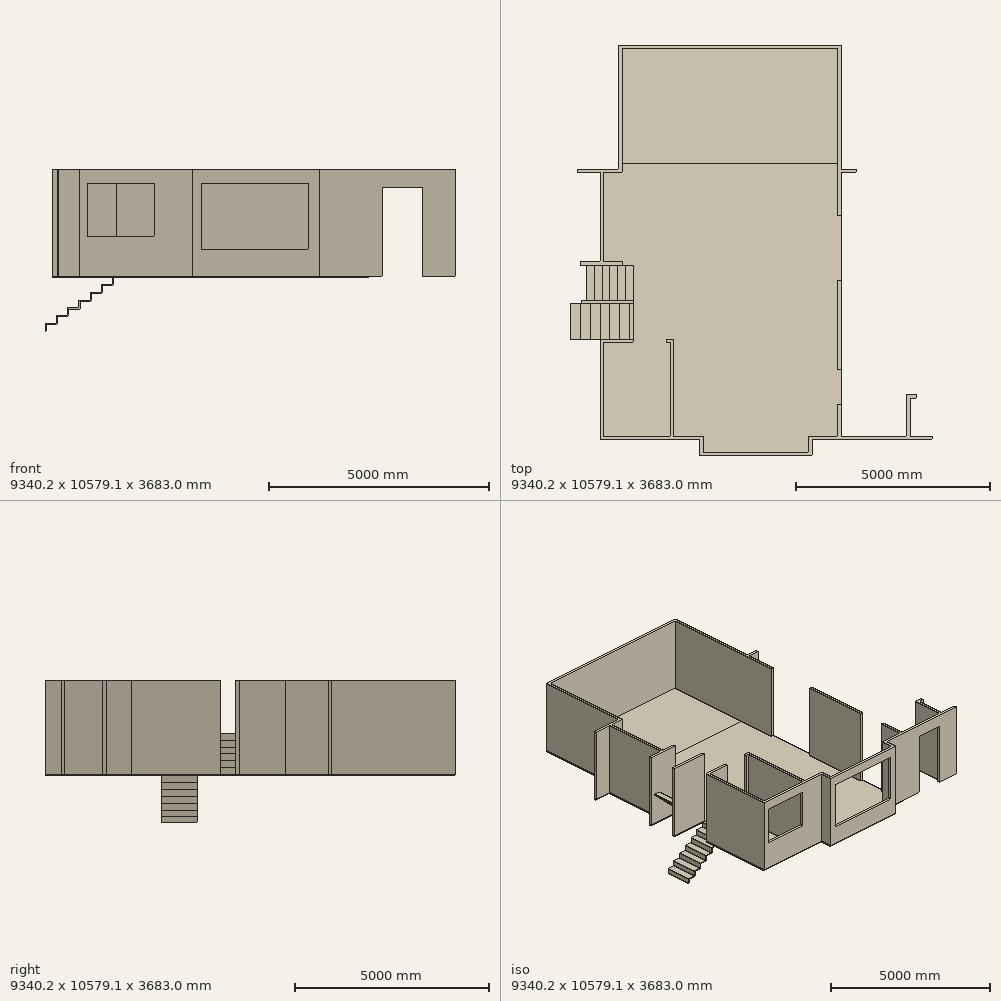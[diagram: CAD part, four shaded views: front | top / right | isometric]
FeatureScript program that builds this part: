
annotation { "Feature Type Name" : "Feature", "Feature Type Description" : "" }
export const myFeature = defineFeature(function(context is Context, id is Id, definition is map)
    precondition{}
    {
        {
            var Q0;
            Q0=qCreatedBy(makeId("Top.planeOp"),FACE);
            var sketch = newSketch(context, id + "F0", { "sketchPlane" : qUnion([Q0])});
            skLineSegment(sketch, "E0", {"start": v(0, 0) * mm, "end": v(0, 2590.8) * mm});
            skLineSegment(sketch, "E1", {"start": v(0, 2590.8) * mm, "end": v(850.9, 2590.8) * mm});
            skLineSegment(sketch, "E2", {"start": v(850.9, 2590.8) * mm, "end": v(850.9, 2501.9) * mm});
            skLineSegment(sketch, "E3", {"start": v(850.9, 2501.9) * mm, "end": v(88.9, 2501.9) * mm});
            skLineSegment(sketch, "E4", {"start": v(88.9, 2501.9) * mm, "end": v(88.9, 88.9) * mm});
            skLineSegment(sketch, "E5", {"start": v(88.9, 88.9) * mm, "end": v(184.15, 88.9) * mm});
            skLineSegment(sketch, "E6", {"start": v(184.15, 88.9) * mm, "end": v(184.15, 0) * mm});
            skLineSegment(sketch, "E7", {"start": v(184.15, 0) * mm, "end": v(0, 0) * mm});
            skLineSegment(sketch, "E8", {"start": v(1708.15, 0) * mm, "end": v(1708.15, 88.9) * mm});
            skLineSegment(sketch, "E9", {"start": v(1708.15, 88.9) * mm, "end": v(1803.4, 88.9) * mm});
            skLineSegment(sketch, "E10", {"start": v(1803.4, 88.9) * mm, "end": v(1803.4, 2501.9) * mm});
            skLineSegment(sketch, "E11", {"start": v(1803.4, 2501.9) * mm, "end": v(1714.5, 2501.9) * mm});
            skLineSegment(sketch, "E12", {"start": v(1714.5, 2501.9) * mm, "end": v(1714.5, 2590.8) * mm});
            skLineSegment(sketch, "E13", {"start": v(1714.5, 2590.8) * mm, "end": v(1892.3, 2590.8) * mm});
            skLineSegment(sketch, "E14", {"start": v(1892.3, 2590.8) * mm, "end": v(1892.3, 88.9) * mm});
            skLineSegment(sketch, "E15", {"start": v(2654.3, -317.5) * mm, "end": v(2654.3, 88.9) * mm});
            skLineSegment(sketch, "E16", {"start": v(2654.3, 88.9) * mm, "end": v(1892.3, 88.9) * mm});
            skLineSegment(sketch, "E17", {"start": v(2654.3, -317.5) * mm, "end": v(2705.1, -317.5) * mm});
            skLineSegment(sketch, "E18", {"start": v(2705.1, -317.5) * mm, "end": v(2705.1, -406.4) * mm});
            skLineSegment(sketch, "E19", {"start": v(2705.1, -406.4) * mm, "end": v(2565.4, -406.4) * mm});
            skLineSegment(sketch, "E20", {"start": v(2565.4, -406.4) * mm, "end": v(2565.4, 0) * mm});
            skLineSegment(sketch, "E21", {"start": v(2565.4, 0) * mm, "end": v(1708.15, 0) * mm});
            skLineSegment(sketch, "E22", {"start": v(184.15, 44.45) * mm, "end": v(1708.15, 44.45) * mm, "construction": true});
            skLineSegment(sketch, "E23", {"start": v(2705.1, -361.95) * mm, "end": v(3924.3, -361.95) * mm, "construction": true});
            skLineSegment(sketch, "E24", {"start": v(4083.05, -361.95) * mm, "end": v(5302.25, -361.95) * mm, "construction": true});
            skLineSegment(sketch, "E25", {"start": v(3924.3, -317.5) * mm, "end": v(4083.05, -317.5) * mm});
            skLineSegment(sketch, "E26", {"start": v(4083.05, -317.5) * mm, "end": v(4083.05, -406.4) * mm});
            skLineSegment(sketch, "E27", {"start": v(4083.05, -406.4) * mm, "end": v(3924.3, -406.4) * mm});
            skLineSegment(sketch, "E28", {"start": v(3924.3, -406.4) * mm, "end": v(3924.3, -317.5) * mm});
            skLineSegment(sketch, "E29", {"start": v(5302.25, -361.95) * mm, "end": v(5302.25, -317.5) * mm});
            skLineSegment(sketch, "E30", {"start": v(5302.25, -317.5) * mm, "end": v(5359.4, -317.5) * mm});
            skLineSegment(sketch, "E31", {"start": v(5359.4, -317.5) * mm, "end": v(5359.4, 88.9) * mm});
            skLineSegment(sketch, "E32", {"start": v(5359.4, 88.9) * mm, "end": v(6121.4, 88.9) * mm});
            skLineSegment(sketch, "E33", {"start": v(6121.4, 88.9) * mm, "end": v(6121.4, 901.7) * mm});
            skLineSegment(sketch, "E34", {"start": v(6121.4, 901.7) * mm, "end": v(6210.3, 901.7) * mm});
            skLineSegment(sketch, "E35", {"start": v(6210.3, 901.7) * mm, "end": v(6210.3, 88.9) * mm});
            skLineSegment(sketch, "E36", {"start": v(6210.3, 88.9) * mm, "end": v(6680.2, 88.9) * mm});
            skLineSegment(sketch, "E37", {"start": v(6680.2, 88.9) * mm, "end": v(6680.2, 0) * mm});
            skLineSegment(sketch, "E38", {"start": v(6680.2, 0) * mm, "end": v(5461, 0) * mm});
            skLineSegment(sketch, "E39", {"start": v(5302.25, -361.95) * mm, "end": v(5302.25, -406.4) * mm});
            skLineSegment(sketch, "E40", {"start": v(5302.25, -406.4) * mm, "end": v(5461, -406.4) * mm});
            skLineSegment(sketch, "E41", {"start": v(5461, -406.4) * mm, "end": v(5461, 0) * mm});
            skLineSegment(sketch, "E42", {"start": v(6680.2, 44.45) * mm, "end": v(7594.6, 44.45) * mm, "construction": true});
            skLineSegment(sketch, "E43", {"start": v(7594.6, 44.45) * mm, "end": v(7594.6, 88.9) * mm});
            skLineSegment(sketch, "E44", {"start": v(7594.6, 88.9) * mm, "end": v(7899.4, 88.9) * mm});
            skLineSegment(sketch, "E45", {"start": v(7899.4, 88.9) * mm, "end": v(7899.4, 1155.7) * mm});
            skLineSegment(sketch, "E46", {"start": v(7899.4, 1155.7) * mm, "end": v(8140.7, 1155.7) * mm});
            skLineSegment(sketch, "E47", {"start": v(8140.7, 1155.7) * mm, "end": v(8140.7, 1066.8) * mm});
            skLineSegment(sketch, "E48", {"start": v(8140.7, 1066.8) * mm, "end": v(7988.3, 1066.8) * mm});
            skLineSegment(sketch, "E49", {"start": v(7988.3, 1066.8) * mm, "end": v(7988.3, 88.9) * mm});
            skLineSegment(sketch, "E50", {"start": v(7988.3, 88.9) * mm, "end": v(8565.55, 88.9) * mm});
            skLineSegment(sketch, "E51", {"start": v(8565.55, 88.9) * mm, "end": v(8565.55, 0) * mm});
            skLineSegment(sketch, "E52", {"start": v(8565.55, 0) * mm, "end": v(7594.6, 0) * mm});
            skLineSegment(sketch, "E53", {"start": v(7594.6, 0) * mm, "end": v(7594.6, 44.45) * mm});
            skLineSegment(sketch, "E54", {"start": v(6165.85, 901.7) * mm, "end": v(6165.85, 1816.1) * mm, "construction": true});
            skLineSegment(sketch, "E55", {"start": v(6165.85, 1816.1) * mm, "end": v(6121.4, 1816.1) * mm});
            skLineSegment(sketch, "E56", {"start": v(6121.4, 1816.1) * mm, "end": v(6121.4, 4102.1) * mm});
            skLineSegment(sketch, "E57", {"start": v(6121.4, 4102.1) * mm, "end": v(6210.3, 4102.1) * mm});
            skLineSegment(sketch, "E58", {"start": v(6210.3, 4102.1) * mm, "end": v(6210.3, 1816.1) * mm});
            skLineSegment(sketch, "E59", {"start": v(6210.3, 1816.1) * mm, "end": v(6165.85, 1816.1) * mm});
            skLineSegment(sketch, "E60", {"start": v(6165.85, 4102.1) * mm, "end": v(6165.85, 5778.5) * mm, "construction": true});
            skLineSegment(sketch, "E61", {"start": v(6165.85, 5778.5) * mm, "end": v(6121.4, 5778.5) * mm});
            skLineSegment(sketch, "E62", {"start": v(6121.4, 5778.5) * mm, "end": v(6121.4, 7200.9) * mm});
            skLineSegment(sketch, "E63", {"start": v(6121.4, 7200.9) * mm, "end": v(6210.3, 7200.9) * mm});
            skLineSegment(sketch, "E64", {"start": v(6210.3, 7200.9) * mm, "end": v(6210.3, 6972.3) * mm});
            skLineSegment(sketch, "E65", {"start": v(6210.3, 6972.3) * mm, "end": v(6608.2, 6972.3) * mm});
            skLineSegment(sketch, "E66", {"start": v(6608.2, 6972.3) * mm, "end": v(6608.2, 6883.4) * mm});
            skLineSegment(sketch, "E67", {"start": v(6608.2, 6883.4) * mm, "end": v(6210.3, 6883.4) * mm});
            skLineSegment(sketch, "E68", {"start": v(6210.3, 6883.4) * mm, "end": v(6210.3, 5778.5) * mm});
            skLineSegment(sketch, "E69", {"start": v(6210.3, 5778.5) * mm, "end": v(6165.85, 5778.5) * mm});
            skLineSegment(sketch, "E70", {"start": v(850.9, 2590.8) * mm, "end": v(850.9, 3505.2) * mm, "construction": true});
            skLineSegment(sketch, "E71", {"start": v(850.9, 3594.1) * mm, "end": v(-482.96, 3594.1) * mm});
            skLineSegment(sketch, "E72", {"start": v(-482.96, 3594.1) * mm, "end": v(-482.96, 3505.2) * mm});
            skLineSegment(sketch, "E73", {"start": v(-482.96, 3505.2) * mm, "end": v(850.9, 3505.2) * mm});
            skLineSegment(sketch, "E74", {"start": v(850.9, 3594.1) * mm, "end": v(850.9, 3505.2) * mm});
            skLineSegment(sketch, "E75", {"start": v(558.8, 3594.1) * mm, "end": v(558.8, 4508.5) * mm, "construction": true});
            skLineSegment(sketch, "E76", {"start": v(558.8, 4508.5) * mm, "end": v(-509.89, 4508.5) * mm});
            skLineSegment(sketch, "E77", {"start": v(-509.89, 4508.5) * mm, "end": v(-509.89, 4597.4) * mm});
            skLineSegment(sketch, "E78", {"start": v(-509.89, 4597.4) * mm, "end": v(0, 4597.4) * mm});
            skLineSegment(sketch, "E79", {"start": v(558.8, 4597.4) * mm, "end": v(558.8, 4508.5) * mm});
            skLineSegment(sketch, "E80", {"start": v(88.9, 4597.4) * mm, "end": v(88.9, 6883.4) * mm});
            skLineSegment(sketch, "E81", {"start": v(88.9, 6883.4) * mm, "end": v(558.8, 6883.4) * mm});
            skLineSegment(sketch, "E82", {"start": v(558.8, 6883.4) * mm, "end": v(558.8, 7200.9) * mm});
            skLineSegment(sketch, "E83", {"start": v(558.8, 7200.9) * mm, "end": v(469.9, 7200.9) * mm});
            skLineSegment(sketch, "E84", {"start": v(469.9, 7200.9) * mm, "end": v(469.9, 6972.3) * mm});
            skLineSegment(sketch, "E85", {"start": v(469.9, 6972.3) * mm, "end": v(-604.12, 6972.3) * mm});
            skLineSegment(sketch, "E86", {"start": v(-604.12, 6972.3) * mm, "end": v(-604.12, 6883.4) * mm});
            skLineSegment(sketch, "E87", {"start": v(-604.12, 6883.4) * mm, "end": v(0, 6883.4) * mm});
            skLineSegment(sketch, "E88", {"start": v(0, 6883.4) * mm, "end": v(0, 4597.4) * mm});
            skLineSegment(sketch, "E89.trimOffspring", {"start": v(88.9, 4597.4) * mm, "end": v(558.8, 4597.4) * mm});
            skLineSegment(sketch, "E90", {"start": v(558.8, 7124.7) * mm, "end": v(6121.4, 7124.7) * mm, "construction": true});
            skLineSegment(sketch, "E91", {"start": v(469.9, 7200.9) * mm, "end": v(469.9, 9029.7) * mm, "construction": true});
            skLineSegment(sketch, "E92", {"start": v(469.9, 9029.7) * mm, "end": v(469.9, 10172.7) * mm});
            skLineSegment(sketch, "E93", {"start": v(558.8, 10083.8) * mm, "end": v(558.8, 9029.7) * mm});
            skLineSegment(sketch, "E94", {"start": v(558.8, 9029.7) * mm, "end": v(469.9, 9029.7) * mm});
            skLineSegment(sketch, "E95", {"start": v(6210.3, 7200.9) * mm, "end": v(6210.3, 9029.7) * mm, "construction": true});
            skLineSegment(sketch, "E96", {"start": v(6210.3, 9029.7) * mm, "end": v(6121.4, 9029.7) * mm});
            skLineSegment(sketch, "E97", {"start": v(6121.4, 9029.7) * mm, "end": v(6121.4, 10083.8) * mm});
            skLineSegment(sketch, "E98", {"start": v(6210.3, 10172.7) * mm, "end": v(6210.3, 9029.7) * mm});
            skLineSegment(sketch, "E99", {"start": v(469.9, 10172.7) * mm, "end": v(6210.3, 10172.7) * mm});
            skLineSegment(sketch, "E100", {"start": v(558.8, 10083.8) * mm, "end": v(6121.4, 10083.8) * mm});
            skLineSegment(sketch, "E101", {"start": v(2705.1, -406.4) * mm, "end": v(5302.25, -406.4) * mm});
            skLineSegment(sketch, "E102", {"start": v(5302.25, -317.5) * mm, "end": v(2705.1, -317.5) * mm});
            skLineSegment(sketch, "E103", {"start": v(1708.15, 0) * mm, "end": v(184.15, 0) * mm});
            skLineSegment(sketch, "E104", {"start": v(1708.15, 88.9) * mm, "end": v(184.15, 88.9) * mm});
            skLineSegment(sketch, "E105", {"start": v(469.9, 7200.9) * mm, "end": v(469.9, 9029.7) * mm});
            skLineSegment(sketch, "E106", {"start": v(558.8, 9029.7) * mm, "end": v(558.8, 7200.9) * mm});
            skLineSegment(sketch, "E107", {"start": v(6121.4, 9029.7) * mm, "end": v(6121.4, 7200.9) * mm});
            skLineSegment(sketch, "E108", {"start": v(6210.3, 7200.9) * mm, "end": v(6210.3, 9029.7) * mm});
            skLineSegment(sketch, "E109", {"start": v(6680.2, 0) * mm, "end": v(7594.6, 0) * mm});
            skLineSegment(sketch, "E110", {"start": v(7594.6, 88.9) * mm, "end": v(6680.2, 88.9) * mm});
            skSolve(sketch);
        }
        {
            var Q0;
            Q0 = qSketchRegion(id + "F0", true);
            extrude(context, id + "F1", {"entities" : qUnion([Q0]), "depth" : 2438.4 * mm});
        }
        {
            var Q0;
            Q0=makeQuery(id+"F1.opExtrude","SWEPT_FACE",FACE,{"disambiguationData":[OSD([sQuery(id+"F0.wireOp",EDGE,"E5"),sQuery(id+"F0.wireOp",EDGE,"E9"),sQuery(id+"F0.wireOp",EDGE,"E104")])]});
            var sketch = newSketch(context, id + "F2", { "sketchPlane" : qUnion([Q0])});
            skLineSegment(sketch, "E111.bottom", {"start": v(-184.15, 2133.6) * mm, "end": v(-1708.15, 2133.6) * mm});
            skLineSegment(sketch, "E111.top", {"start": v(-1708.15, 914.4) * mm, "end": v(-184.15, 914.4) * mm});
            skLineSegment(sketch, "E111.left", {"start": v(-184.15, 2133.6) * mm, "end": v(-184.15, 914.4) * mm});
            skLineSegment(sketch, "E111.right", {"start": v(-1708.15, 2133.6) * mm, "end": v(-1708.15, 914.4) * mm});
            skLineSegment(sketch, "E112.0", {"start": v(-88.9, 2438.4) * mm, "end": v(-88.9, 0) * mm});
            skLineSegment(sketch, "E113.0", {"start": v(-1803.4, 2438.4) * mm, "end": v(-1803.4, 0) * mm});
            skLineSegment(sketch, "E114.0", {"start": v(-88.9, 0) * mm, "end": v(-1803.4, 0) * mm});
            skLineSegment(sketch, "E115", {"start": v(-184.15, 2133.6) * mm, "end": v(-88.9, 2133.6) * mm, "construction": true});
            skLineSegment(sketch, "E116", {"start": v(-1708.15, 2133.6) * mm, "end": v(-1803.4, 2133.6) * mm, "construction": true});
            skSolve(sketch);
        }
        {
            var Q0;
            Q0 = qSketchRegion(id + "F2", true);
            extrude(context, id + "F3", {"entities" : qUnion([Q0]), "operationType" : NewBodyOperationType.REMOVE, "endBound" : BoundingType.THROUGH_ALL, "oppositeDirection" : true, "depth" : 25.4 * mm});
        }
        {
            var Q0;
            Q0=makeQuery(id+"F1.opExtrude","SWEPT_FACE",FACE,{"disambiguationData":[OSD([sQuery(id+"F0.wireOp",EDGE,"E17"),sQuery(id+"F0.wireOp",EDGE,"E30"),sQuery(id+"F0.wireOp",EDGE,"E102")])]});
            var sketch = newSketch(context, id + "F4", { "sketchPlane" : qUnion([Q0])});
            skLineSegment(sketch, "E117.bottom", {"start": v(-5226.05, 2133.6) * mm, "end": v(-2787.65, 2133.6) * mm});
            skLineSegment(sketch, "E117.top", {"start": v(-5226.05, 609.6) * mm, "end": v(-2787.65, 609.6) * mm});
            skLineSegment(sketch, "E117.left", {"start": v(-5226.05, 2133.6) * mm, "end": v(-5226.05, 609.6) * mm});
            skLineSegment(sketch, "E117.right", {"start": v(-2787.65, 2133.6) * mm, "end": v(-2787.65, 609.6) * mm});
            skLineSegment(sketch, "E118", {"start": v(-2787.65, 2133.6) * mm, "end": v(-2654.3, 2133.6) * mm, "construction": true});
            skLineSegment(sketch, "E119", {"start": v(-5226.05, 2133.6) * mm, "end": v(-5359.4, 2133.6) * mm, "construction": true});
            skSolve(sketch);
        }
        {
            var Q0;
            Q0 = qSketchRegion(id + "F4", true);
            extrude(context, id + "F5", {"entities" : qUnion([Q0]), "operationType" : NewBodyOperationType.REMOVE, "endBound" : BoundingType.THROUGH_ALL, "oppositeDirection" : true, "depth" : 25.4 * mm});
        }
        {
            var Q0;
            Q0=makeQuery(id+"F1.opExtrude","SWEPT_FACE",FACE,{"disambiguationData":[OSD([sQuery(id+"F0.wireOp",EDGE,"E36"),sQuery(id+"F0.wireOp",EDGE,"E44"),sQuery(id+"F0.wireOp",EDGE,"E110")])]});
            var sketch = newSketch(context, id + "F6", { "sketchPlane" : qUnion([Q0])});
            skLineSegment(sketch, "E120.bottom", {"start": v(-7823.2, 0) * mm, "end": v(-6908.8, 0) * mm});
            skLineSegment(sketch, "E120.top", {"start": v(-7823.2, 2032) * mm, "end": v(-6908.8, 2032) * mm});
            skLineSegment(sketch, "E120.left", {"start": v(-7823.2, 0) * mm, "end": v(-7823.2, 2032) * mm});
            skLineSegment(sketch, "E120.right", {"start": v(-6908.8, 0) * mm, "end": v(-6908.8, 2032) * mm});
            skSolve(sketch);
        }
        {
            var Q0;
            Q0 = qSketchRegion(id + "F6", true);
            extrude(context, id + "F7", {"entities" : qUnion([Q0]), "operationType" : NewBodyOperationType.REMOVE, "endBound" : BoundingType.THROUGH_ALL, "oppositeDirection" : true, "depth" : 25.4 * mm});
        }
        {
            var Q0;
            Q0=makeQuery(id+"F1.opExtrude","SWEPT_FACE",FACE,{"disambiguationData":[OSD([sQuery(id+"F0.wireOp",EDGE,"E73")])]});
            var sketch = newSketch(context, id + "F8", { "sketchPlane" : qUnion([Q0])});
            skLineSegment(sketch, "E121", {"start": v(850.9, 0) * mm, "end": v(749.3, 0) * mm});
            skLineSegment(sketch, "E122", {"start": v(749.3, 0) * mm, "end": v(749.3, -177.8) * mm});
            skLineSegment(sketch, "E123", {"start": v(749.3, -177.8) * mm, "end": v(495.3, -177.8) * mm});
            skLineSegment(sketch, "E124", {"start": v(850.9, 0) * mm, "end": v(850.9, -25.4) * mm});
            skLineSegment(sketch, "E125", {"start": v(495.3, -177.8) * mm, "end": v(495.3, -355.6) * mm});
            skLineSegment(sketch, "E126", {"start": v(495.3, -355.6) * mm, "end": v(241.3, -355.6) * mm});
            skLineSegment(sketch, "E127", {"start": v(241.3, -355.6) * mm, "end": v(241.3, -533.4) * mm});
            skLineSegment(sketch, "E128", {"start": v(241.3, -533.4) * mm, "end": v(-12.7, -533.4) * mm});
            skLineSegment(sketch, "E129", {"start": v(-12.7, -533.4) * mm, "end": v(-12.7, -711.2) * mm});
            skLineSegment(sketch, "E130", {"start": v(-12.7, -711.2) * mm, "end": v(-266.7, -711.2) * mm});
            skLineSegment(sketch, "E131", {"start": v(-266.7, -711.2) * mm, "end": v(-266.7, -889) * mm});
            skLineSegment(sketch, "E132", {"start": v(-266.7, -889) * mm, "end": v(-520.7, -889) * mm});
            skLineSegment(sketch, "E133", {"start": v(-520.7, -889) * mm, "end": v(-520.7, -1066.8) * mm});
            skLineSegment(sketch, "E134", {"start": v(-520.7, -1066.8) * mm, "end": v(-774.7, -1066.8) * mm});
            skLineSegment(sketch, "E135", {"start": v(-774.7, -1066.8) * mm, "end": v(-774.7, -1244.6) * mm});
            skLineSegment(sketch, "E136", {"start": v(-774.7, -1244.6) * mm, "end": v(-749.3, -1244.6) * mm});
            skLineSegment(sketch, "E137", {"start": v(-749.3, -1244.6) * mm, "end": v(-749.3, -1092.2) * mm});
            skLineSegment(sketch, "E138", {"start": v(-749.3, -1092.2) * mm, "end": v(-495.3, -1092.2) * mm});
            skLineSegment(sketch, "E139", {"start": v(-495.3, -1092.2) * mm, "end": v(-495.3, -914.4) * mm});
            skLineSegment(sketch, "E140", {"start": v(-495.3, -914.4) * mm, "end": v(-241.3, -914.4) * mm});
            skLineSegment(sketch, "E141", {"start": v(-241.3, -914.4) * mm, "end": v(-241.3, -736.6) * mm});
            skLineSegment(sketch, "E142", {"start": v(-241.3, -736.6) * mm, "end": v(12.7, -736.6) * mm});
            skLineSegment(sketch, "E143", {"start": v(12.7, -736.6) * mm, "end": v(12.7, -558.8) * mm});
            skLineSegment(sketch, "E144", {"start": v(12.7, -558.8) * mm, "end": v(266.7, -558.8) * mm});
            skLineSegment(sketch, "E145", {"start": v(266.7, -558.8) * mm, "end": v(266.7, -381) * mm});
            skLineSegment(sketch, "E146", {"start": v(266.7, -381) * mm, "end": v(520.7, -381) * mm});
            skLineSegment(sketch, "E147", {"start": v(520.7, -381) * mm, "end": v(520.7, -203.2) * mm});
            skLineSegment(sketch, "E148", {"start": v(520.7, -203.2) * mm, "end": v(774.7, -203.2) * mm});
            skLineSegment(sketch, "E149", {"start": v(774.7, -203.2) * mm, "end": v(774.7, -25.4) * mm});
            skLineSegment(sketch, "E150", {"start": v(774.7, -25.4) * mm, "end": v(850.9, -25.4) * mm});
            skSolve(sketch);
        }
        {
            var Q0;
            Q0 = qSketchRegion(id + "F8", true);
            extrude(context, id + "F9", {"entities" : qUnion([Q0]), "depth" : 914.4 * mm});
        }
        {
            var Q0;
            {var subQ0=sQuery(id+"F0.wireOp",EDGE,"E34");var subQ1=sQuery(id+"F0.wireOp",EDGE,"E33");var subQ2=sQuery(id+"F0.wireOp",EDGE,"E32");var subQ3=sQuery(id+"F0.wireOp",EDGE,"E31");var subQ4=sQuery(id+"F0.wireOp",EDGE,"E20");var subQ5=sQuery(id+"F0.wireOp",EDGE,"E101");var subQ6=sQuery(id+"F0.wireOp",EDGE,"E40");var subQ7=sQuery(id+"F0.wireOp",EDGE,"E19");var subQ8=sQuery(id+"F0.wireOp",EDGE,"E102");var subQ9=sQuery(id+"F0.wireOp",EDGE,"E30");var subQ10=sQuery(id+"F0.wireOp",EDGE,"E17");var subQ11=sQuery(id+"F0.wireOp",EDGE,"E16");var subQ12=sQuery(id+"F0.wireOp",EDGE,"E15");var subQ13=sQuery(id+"F0.wireOp",EDGE,"E14");var subQ14=sQuery(id+"F0.wireOp",EDGE,"E13");var subQ15=sQuery(id+"F0.wireOp",EDGE,"E2");var subQ16=sQuery(id+"F0.wireOp",EDGE,"E1");var subQ17=sQuery(id+"F0.wireOp",EDGE,"E3");var subQ18=sQuery(id+"F0.wireOp",EDGE,"E35");var subQ19=sQuery(id+"F0.wireOp",EDGE,"E0");var subQ20=sQuery(id+"F0.wireOp",EDGE,"E12");var subQ21=sQuery(id+"F0.wireOp",EDGE,"E4");var subQ22=sQuery(id+"F0.wireOp",EDGE,"E104");var subQ23=sQuery(id+"F0.wireOp",EDGE,"E9");var subQ24=sQuery(id+"F0.wireOp",EDGE,"E5");var subQ25=sQuery(id+"F0.wireOp",EDGE,"E103");var subQ26=sQuery(id+"F0.wireOp",EDGE,"E21");var subQ27=sQuery(id+"F0.wireOp",EDGE,"E7");var subQ28=sQuery(id+"F0.wireOp",EDGE,"E10");var subQ29=sQuery(id+"F0.wireOp",EDGE,"E11");var subQ30=sQuery(id+"F0.wireOp",EDGE,"E110");var subQ31=sQuery(id+"F0.wireOp",EDGE,"E44");var subQ32=sQuery(id+"F0.wireOp",EDGE,"E36");var subQ33=sQuery(id+"F0.wireOp",EDGE,"E109");var subQ34=sQuery(id+"F0.wireOp",EDGE,"E52");var subQ35=sQuery(id+"F0.wireOp",EDGE,"E38");var subQ36=sQuery(id+"F0.wireOp",EDGE,"E41");Q0=makeQuery(id+"F7.boolean.opBoolean","SPLIT",FACE,{"disambiguationData":[TD([makeQuery(id+"F1.opExtrude","SWEPT_FACE",FACE,{"disambiguationData":[OSD([subQ19])]})])],"derivedFrom":makeQuery(id+"F1.opExtrude","CAP_FACE",FACE,{"disambiguationData":[OSD([subQ19,subQ16,subQ15,subQ17,subQ21,subQ24,subQ27,subQ23,subQ28,subQ29,subQ20,subQ14,subQ13,subQ12,subQ11,subQ10,subQ7,subQ4,subQ26,subQ9,subQ3,subQ2,subQ1,subQ0,subQ18,subQ32,subQ35,subQ6,subQ36,subQ31,sQuery(id+"F0.wireOp",EDGE,"E45"),sQuery(id+"F0.wireOp",EDGE,"E46"),sQuery(id+"F0.wireOp",EDGE,"E47"),sQuery(id+"F0.wireOp",EDGE,"E48"),sQuery(id+"F0.wireOp",EDGE,"E49"),sQuery(id+"F0.wireOp",EDGE,"E50"),sQuery(id+"F0.wireOp",EDGE,"E51"),subQ34,subQ5,subQ8,subQ25,subQ22,subQ33,subQ30])],"isStart":true})});}
            var sketch = newSketch(context, id + "F10", { "sketchPlane" : qUnion([Q0])});
            skLineSegment(sketch, "E151", {"start": v(0, 0) * mm, "end": v(2565.4, 0) * mm});
            skLineSegment(sketch, "E152", {"start": v(2565.4, 0) * mm, "end": v(2565.4, 406.4) * mm});
            skLineSegment(sketch, "E153", {"start": v(2565.4, 406.4) * mm, "end": v(5461, 406.4) * mm});
            skLineSegment(sketch, "E154", {"start": v(5461, 406.4) * mm, "end": v(5461, 0) * mm});
            skLineSegment(sketch, "E155", {"start": v(5461, 0) * mm, "end": v(6210.3, 0) * mm});
            skLineSegment(sketch, "E156.0.0", {"start": v(6210.3, -5778.5) * mm, "end": v(6121.4, -5778.5) * mm});
            skLineSegment(sketch, "E156.0.4", {"start": v(558.8, -6883.4) * mm, "end": v(88.9, -6883.4) * mm});
            skLineSegment(sketch, "E156.0.5", {"start": v(88.9, -6883.4) * mm, "end": v(88.9, -4597.4) * mm});
            skLineSegment(sketch, "E156.0.6", {"start": v(88.9, -4597.4) * mm, "end": v(558.8, -4597.4) * mm});
            skLineSegment(sketch, "E156.0.7", {"start": v(558.8, -4597.4) * mm, "end": v(558.8, -4508.5) * mm});
            skLineSegment(sketch, "E156.0.8", {"start": v(558.8, -4508.5) * mm, "end": v(-509.89, -4508.5) * mm});
            skLineSegment(sketch, "E156.0.9", {"start": v(-509.89, -4508.5) * mm, "end": v(-509.89, -4597.4) * mm});
            skLineSegment(sketch, "E156.0.10", {"start": v(-509.89, -4597.4) * mm, "end": v(0, -4597.4) * mm});
            skLineSegment(sketch, "E156.0.11", {"start": v(0, -4597.4) * mm, "end": v(0, -6883.4) * mm});
            skLineSegment(sketch, "E156.0.12", {"start": v(0, -6883.4) * mm, "end": v(-604.12, -6883.4) * mm});
            skLineSegment(sketch, "E156.0.13", {"start": v(-604.12, -6883.4) * mm, "end": v(-604.12, -6972.3) * mm});
            skLineSegment(sketch, "E156.0.14", {"start": v(-604.12, -6972.3) * mm, "end": v(469.9, -6972.3) * mm});
            skLineSegment(sketch, "E156.0.18", {"start": v(6210.3, -6972.3) * mm, "end": v(6608.2, -6972.3) * mm});
            skLineSegment(sketch, "E156.0.19", {"start": v(6608.2, -6972.3) * mm, "end": v(6608.2, -6883.4) * mm});
            skLineSegment(sketch, "E156.0.20", {"start": v(6608.2, -6883.4) * mm, "end": v(6210.3, -6883.4) * mm});
            skLineSegment(sketch, "E156.0.21", {"start": v(6210.3, -6883.4) * mm, "end": v(6210.3, -5778.5) * mm});
            skLineSegment(sketch, "E157", {"start": v(88.9, -6972.3) * mm, "end": v(88.9, -4597.4) * mm});
            skLineSegment(sketch, "E158.0.0", {"start": v(850.9, -3594.1) * mm, "end": v(850.9, -3505.2) * mm});
            skLineSegment(sketch, "E158.0.1", {"start": v(850.9, -3505.2) * mm, "end": v(-482.96, -3505.2) * mm});
            skLineSegment(sketch, "E158.0.2", {"start": v(-482.96, -3505.2) * mm, "end": v(-482.96, -3594.1) * mm});
            skLineSegment(sketch, "E158.0.3", {"start": v(-482.96, -3594.1) * mm, "end": v(850.9, -3594.1) * mm});
            skLineSegment(sketch, "E159", {"start": v(558.8, -4508.5) * mm, "end": v(558.8, -3594.1) * mm});
            skLineSegment(sketch, "E160", {"start": v(558.8, -3594.1) * mm, "end": v(850.9, -3594.1) * mm});
            skLineSegment(sketch, "E161", {"start": v(0, 0) * mm, "end": v(0, -2590.8) * mm});
            skLineSegment(sketch, "E162", {"start": v(0, -2590.8) * mm, "end": v(850.9, -2590.8) * mm});
            skLineSegment(sketch, "E163", {"start": v(850.9, -2590.8) * mm, "end": v(850.9, -3594.1) * mm});
            skLineSegment(sketch, "E164", {"start": v(469.9, -6972.3) * mm, "end": v(469.9, -7124.7) * mm});
            skLineSegment(sketch, "E165", {"start": v(469.9, -7124.7) * mm, "end": v(6210.3, -7124.7) * mm});
            skLineSegment(sketch, "E166", {"start": v(6210.3, -7124.7) * mm, "end": v(6210.3, -6972.3) * mm});
            skLineSegment(sketch, "E167", {"start": v(6210.3, 0) * mm, "end": v(6210.3, -7124.7) * mm});
            skSolve(sketch);
        }
        {
            var Q0;
            Q0 = qSketchRegion(id + "F10", true);
            extrude(context, id + "F11", {"entities" : qUnion([Q0]), "depth" : 25.4 * mm});
        }
        {
            var Q0;
            Q0=makeQuery(id+"F1.opExtrude","CAP_FACE",FACE,{"disambiguationData":[OSD([sQuery(id+"F0.wireOp",EDGE,"E61"),sQuery(id+"F0.wireOp",EDGE,"E62"),sQuery(id+"F0.wireOp",EDGE,"E64"),sQuery(id+"F0.wireOp",EDGE,"E65"),sQuery(id+"F0.wireOp",EDGE,"E66"),sQuery(id+"F0.wireOp",EDGE,"E67"),sQuery(id+"F0.wireOp",EDGE,"E68"),sQuery(id+"F0.wireOp",EDGE,"E69"),sQuery(id+"F0.wireOp",EDGE,"E76"),sQuery(id+"F0.wireOp",EDGE,"E77"),sQuery(id+"F0.wireOp",EDGE,"E78"),sQuery(id+"F0.wireOp",EDGE,"E79"),sQuery(id+"F0.wireOp",EDGE,"E80"),sQuery(id+"F0.wireOp",EDGE,"E81"),sQuery(id+"F0.wireOp",EDGE,"E82"),sQuery(id+"F0.wireOp",EDGE,"E84"),sQuery(id+"F0.wireOp",EDGE,"E85"),sQuery(id+"F0.wireOp",EDGE,"E86"),sQuery(id+"F0.wireOp",EDGE,"E87"),sQuery(id+"F0.wireOp",EDGE,"E88"),sQuery(id+"F0.wireOp",EDGE,"E89.trimOffspring"),sQuery(id+"F0.wireOp",EDGE,"E92"),sQuery(id+"F0.wireOp",EDGE,"E93"),sQuery(id+"F0.wireOp",EDGE,"E97"),sQuery(id+"F0.wireOp",EDGE,"E98"),sQuery(id+"F0.wireOp",EDGE,"E99"),sQuery(id+"F0.wireOp",EDGE,"E100"),sQuery(id+"F0.wireOp",EDGE,"E105"),sQuery(id+"F0.wireOp",EDGE,"E106"),sQuery(id+"F0.wireOp",EDGE,"E107"),sQuery(id+"F0.wireOp",EDGE,"E108")])],"isStart":true});
            var sketch = newSketch(context, id + "F12", { "sketchPlane" : qUnion([Q0])});
            skLineSegment(sketch, "E168.0", {"start": v(469.9, -7124.7) * mm, "end": v(6210.3, -7124.7) * mm});
            skLineSegment(sketch, "E169", {"start": v(469.9, -7124.7) * mm, "end": v(469.9, -10172.7) * mm});
            skLineSegment(sketch, "E170", {"start": v(469.9, -10172.7) * mm, "end": v(6210.3, -10172.7) * mm});
            skLineSegment(sketch, "E171", {"start": v(6210.3, -10172.7) * mm, "end": v(6210.3, -7124.7) * mm});
            skSolve(sketch);
        }
        {
            var Q0;
            Q0 = qSketchRegion(id + "F12", true);
            extrude(context, id + "F13", {"entities" : qUnion([Q0]), "depth" : 25.4 * mm});
        }
        {
            var Q0;
            Q0=makeQuery(id+"F1.opExtrude","SWEPT_FACE",FACE,{"disambiguationData":[OSD([sQuery(id+"F0.wireOp",EDGE,"E71")])]});
            var sketch = newSketch(context, id + "F14", { "sketchPlane" : qUnion([Q0])});
            skLineSegment(sketch, "E172", {"start": v(-850.9, 0) * mm, "end": v(-850.9, 177.8) * mm});
            skLineSegment(sketch, "E173", {"start": v(-850.9, 177.8) * mm, "end": v(-647.7, 177.8) * mm});
            skLineSegment(sketch, "E174", {"start": v(-647.7, 177.8) * mm, "end": v(-647.7, 355.6) * mm});
            skLineSegment(sketch, "E175", {"start": v(-647.7, 355.6) * mm, "end": v(-444.5, 355.6) * mm});
            skLineSegment(sketch, "E176", {"start": v(-444.5, 355.6) * mm, "end": v(-444.5, 533.4) * mm});
            skLineSegment(sketch, "E177", {"start": v(-444.5, 533.4) * mm, "end": v(-241.3, 533.4) * mm});
            skLineSegment(sketch, "E178", {"start": v(-241.3, 533.4) * mm, "end": v(-241.3, 711.2) * mm});
            skLineSegment(sketch, "E179", {"start": v(-241.3, 711.2) * mm, "end": v(-38.1, 711.2) * mm});
            skLineSegment(sketch, "E180", {"start": v(-38.1, 711.2) * mm, "end": v(-38.1, 889) * mm});
            skLineSegment(sketch, "E181", {"start": v(-38.1, 889) * mm, "end": v(165.1, 889) * mm});
            skLineSegment(sketch, "E182", {"start": v(165.1, 889) * mm, "end": v(165.1, 1066.8) * mm});
            skLineSegment(sketch, "E183", {"start": v(165.1, 1066.8) * mm, "end": v(368.3, 1066.8) * mm});
            skLineSegment(sketch, "E184", {"start": v(368.3, 1066.8) * mm, "end": v(368.3, 1041.4) * mm});
            skLineSegment(sketch, "E185", {"start": v(368.3, 1041.4) * mm, "end": v(190.5, 1041.4) * mm});
            skLineSegment(sketch, "E186", {"start": v(190.5, 1041.4) * mm, "end": v(190.5, 863.6) * mm});
            skLineSegment(sketch, "E187", {"start": v(190.5, 863.6) * mm, "end": v(-12.7, 863.6) * mm});
            skLineSegment(sketch, "E188", {"start": v(-12.7, 863.6) * mm, "end": v(-12.7, 685.8) * mm});
            skLineSegment(sketch, "E189", {"start": v(-12.7, 685.8) * mm, "end": v(-215.9, 685.8) * mm});
            skLineSegment(sketch, "E190", {"start": v(-215.9, 685.8) * mm, "end": v(-215.9, 508) * mm});
            skLineSegment(sketch, "E191", {"start": v(-215.9, 508) * mm, "end": v(-419.1, 508) * mm});
            skLineSegment(sketch, "E192", {"start": v(-419.1, 508) * mm, "end": v(-419.1, 330.2) * mm});
            skLineSegment(sketch, "E193", {"start": v(-419.1, 330.2) * mm, "end": v(-622.3, 330.2) * mm});
            skLineSegment(sketch, "E194", {"start": v(-622.3, 330.2) * mm, "end": v(-622.3, 152.4) * mm});
            skLineSegment(sketch, "E195", {"start": v(-622.3, 152.4) * mm, "end": v(-825.5, 152.4) * mm});
            skLineSegment(sketch, "E196", {"start": v(-825.5, 152.4) * mm, "end": v(-825.5, 0) * mm});
            skLineSegment(sketch, "E197", {"start": v(-825.5, 0) * mm, "end": v(-850.9, 0) * mm});
            skSolve(sketch);
        }
        {
            var Q0;
            Q0 = qSketchRegion(id + "F14", true);
            extrude(context, id + "F15", {"entities" : qUnion([Q0]), "depth" : 914.4 * mm});
        }
    });
